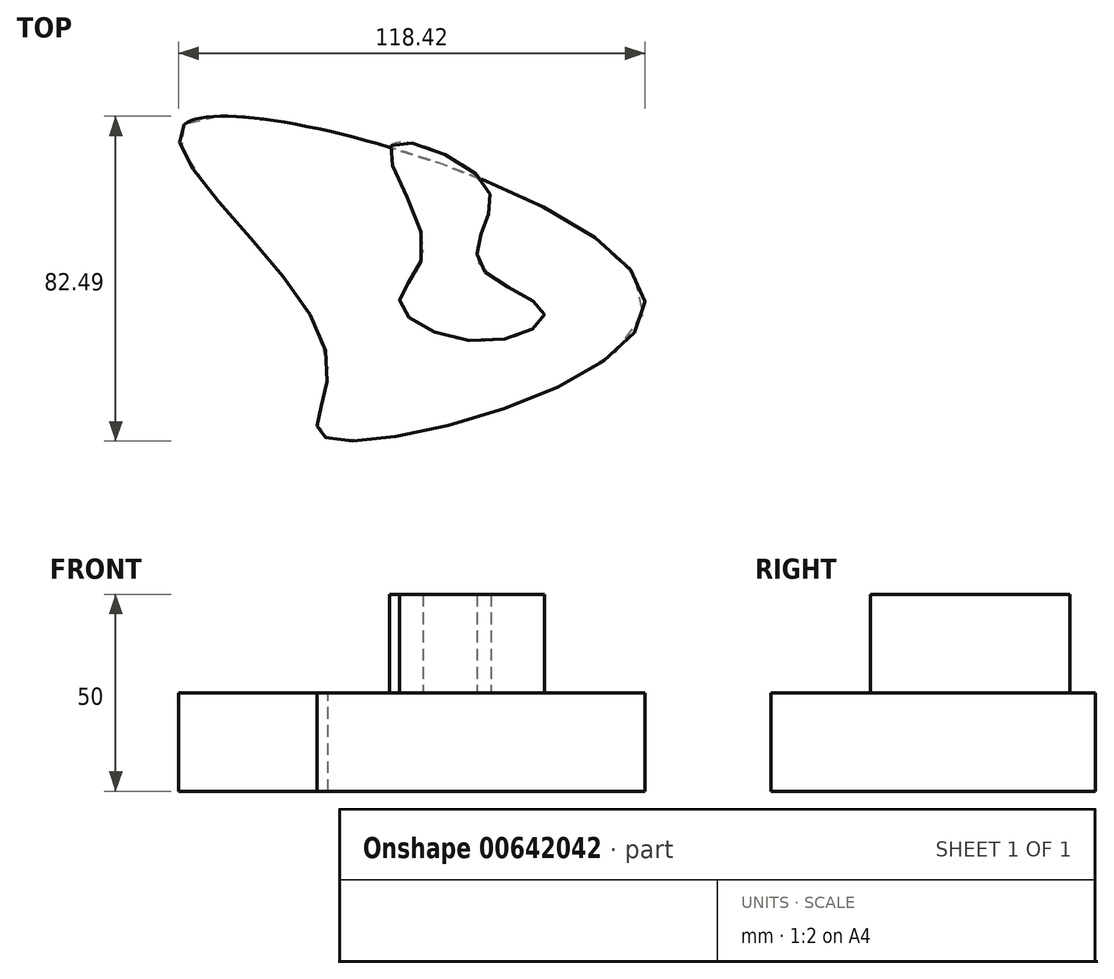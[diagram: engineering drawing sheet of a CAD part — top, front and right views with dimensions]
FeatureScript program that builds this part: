
annotation { "Feature Type Name" : "Feature", "Feature Type Description" : "" }
export const myFeature = defineFeature(function(context is Context, id is Id, definition is map)
    precondition{}
    {
        {
            var Q0;
            Q0=qCreatedBy(makeId("Top.planeOp"),FACE);
            var sketch = newSketch(context, id + "F0", { "sketchPlane" : qUnion([Q0])});
            skFitSpline(sketch, "E0", {"points": [v(-76.15, 79.52) * mm, v(-40.12, 22.2) * mm, v(-40.16, 0) * mm, v(40.95, 34.56) * mm, v(-76.15, 79.52) * mm]});
            skSolve(sketch);
        }
        {
            var Q0;
            Q0 = qSketchRegion(id + "F0", true);
            extrude(context, id + "F1", {"entities" : qUnion([Q0]), "depth" : 25 * mm, "offsetDistance" : 25 * mm});
        }
        {
            var Q0;
            Q0=makeQuery(id+"F1.opExtrude","CAP_FACE",FACE,{"disambiguationData":[OSD([sQuery(id+"F0.wireOp",EDGE,"E0")])],"isStart":false});
            var sketch = newSketch(context, id + "F2", { "sketchPlane" : qUnion([Q0])});
            skSolve(sketch);
        }
        {
            var Q0;
            Q0=makeQuery(id+"F2.imprint","IMPRINT",FACE,{"disambiguationData":[TD([[makeQuery(id+"F2.imprint","IMPRINT",EDGE,{"derivedFrom":makeQuery(id+"F1.opExtrude","CAP_EDGE",EDGE,{"disambiguationData":[OSD([sQuery(id+"F0.wireOp",EDGE,"E0")])],"isStart":false})}),1.0]])]});
            var sketch = newSketch(context, id + "F3", { "sketchPlane" : qUnion([Q0])});
            skFitSpline(sketch, "E1", {"points": [v(-23.46, 74.26) * mm, v(-15.35, 48.14) * mm, v(-21.34, 34.38) * mm, v(0, 24.5) * mm, v(15.36, 31.9) * mm, v(0, 42.5) * mm, v(0, 53.43) * mm, v(0, 65.08) * mm, v(-23.46, 74.26) * mm]});
            skSolve(sketch);
        }
        {
            var Q0;
            Q0 = qSketchRegion(id + "F3", true);
            extrude(context, id + "F4", {"entities" : qUnion([Q0]), "operationType" : NewBodyOperationType.ADD, "depth" : 25 * mm, "offsetDistance" : 25 * mm});
        }
    });
